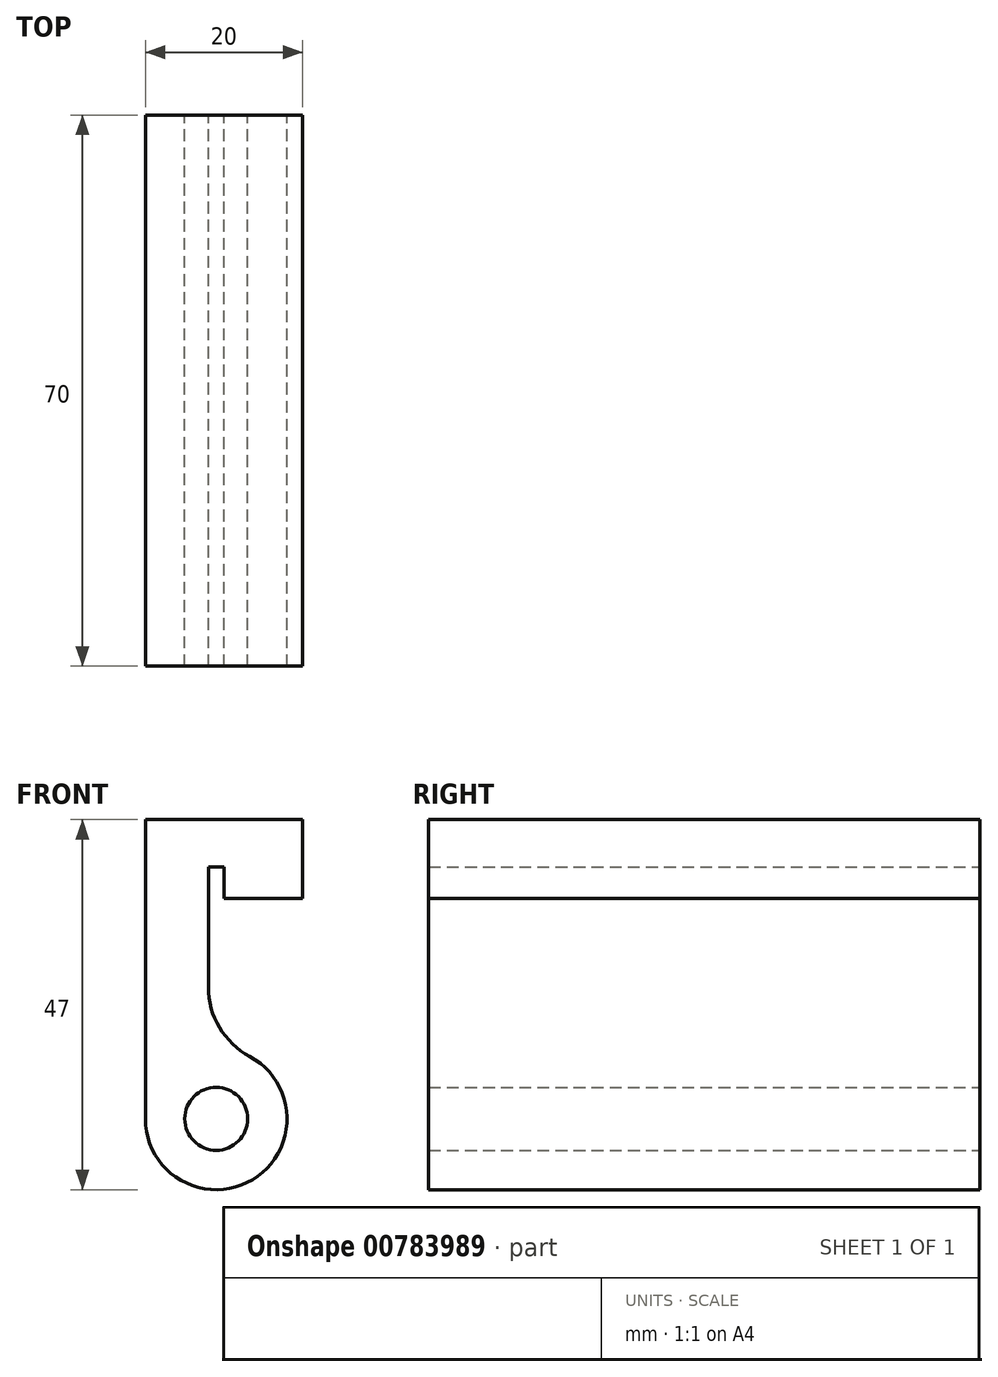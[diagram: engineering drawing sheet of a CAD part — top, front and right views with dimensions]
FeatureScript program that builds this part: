
annotation { "Feature Type Name" : "Feature", "Feature Type Description" : "" }
export const myFeature = defineFeature(function(context is Context, id is Id, definition is map)
    precondition{}
    {
        {
            var Q0;
            Q0=qCreatedBy(makeId("Front.planeOp"),FACE);
            var sketch = newSketch(context, id + "F0", { "sketchPlane" : qUnion([Q0])});
            skCircle(sketch, "E0", {"center": v(0, 0) * mm, "radius": 4 * mm});
            skCircle(sketch, "E1", {"center": v(0, 0) * mm, "radius": 9 * mm});
            skLineSegment(sketch, "E2", {"start": v(-9, 0) * mm, "end": v(-9, 38) * mm});
            skLineSegment(sketch, "E3", {"start": v(-9, 38) * mm, "end": v(11, 38) * mm});
            skLineSegment(sketch, "E4", {"start": v(11, 38) * mm, "end": v(11, 28) * mm});
            skLineSegment(sketch, "E5", {"start": v(11, 28) * mm, "end": v(1, 28) * mm});
            skLineSegment(sketch, "E6", {"start": v(1, 28) * mm, "end": v(1, 32) * mm});
            skLineSegment(sketch, "E7", {"start": v(1, 32) * mm, "end": v(-1, 32) * mm});
            skLineSegment(sketch, "E8", {"start": v(-1, 32) * mm, "end": v(-1, 8.94) * mm});
            skSolve(sketch);
        }
        {
            var Q0;
            {var subQ0=sQuery(id+"F0.wireOp",EDGE,"E2");Q0=makeQuery(id+"F0.imprint","IMPRINT",FACE,{"disambiguationData":[TD([[makeQuery(id+"F0.imprint","IMPRINT",EDGE,{"derivedFrom":subQ0}),-1.0]])]});}
            var Q1;
            Q1=makeQuery(id+"F0.imprint","IMPRINT",FACE,{"disambiguationData":[TD([[makeQuery(id+"F0.imprint","IMPRINT",EDGE,{"derivedFrom":sQuery(id+"F0.wireOp",EDGE,"E0")}),-1.0]])]});
            extrude(context, id + "F1", {"entities" : qUnion([Q0, Q1]), "depth" : 70 * mm, "offsetDistance" : 25 * mm});
        }
        {
            var Q0;
            Q0=makeQuery(id+"F1.opExtrude","SWEPT_EDGE",EDGE,{"disambiguationData":[OSD([sQuery(id+"F0.wireOp",EDGE,"E1"),sQuery(id+"F0.wireOp",EDGE,"E8")])]});
            fillet(context, id + "F2", {"entities" : qUnion([Q0]), "radius" : 10 * mm, "tangentPropagation" : true, "allowEdgeOverflow" : false});
        }
    });
